# Revit family: Oil_Interceptors-Integral_Storage_Compartment-Jay R. Smith-8599_Series
name_source: partatom
category: Specialty Equipment
units: mm (PartAtom-declared; Revit-internal decimal feet)

## family parameters
Cut with Voids When Loaded = No
Host = Face
OmniClass Number = 23.70.50.11.14.11
OmniClass Title = Oil-Water Separators
Part Type = Normal
Room Calculation Point = No
Round Connector Dimension = Use Diameter
Shared = No

## types (17) — shared parameters
4"(100) Cleanout Access = No
Assembly Code = D2090300
CW Connection = No
Default Elevation = 0"
Description = Oil Interceptors with Integral Storage Compartment
Double Wall Containment - DWC (Note 1) = No
Extension -E (Specify Height eg -E12 for 12" ext.) = No
Finish = Steel-Jay R. Smith-Fabricated
HW Connection = No
High Level Sensor and Control Panel -CBS = No
Installation Type = Floor Mounted
Manufacturer = Jay R. Smith
Manufacturer Product Line = Drainage Products
Material = Steel-Jay R. Smith-Fabricated
Product Documentation Link = https://www.jrsmith.com
Product Page URL = https://www.jrsmith.com
R1 = 2"
Traffic Rated Cover -H20 = No
URL = https://www.jrsmith.com
Vent Connection = No
Vent Connection Diameter = 3"
Waste Connection = Yes

## per-type parameters (varying)
| type | A Dimension | B Dimension | C Dimension | Capacity | D Dimension | E Dimension | F Dimension | Flow Rate | G Dimension | H Dimension | Inlet Connection Description | Inlet Connection Diameter | Inlet/Outlet Radius | J Dimension | M Dimension | Model | N Dimension | Outlet Connection Description | Outlet Connection Diameter | P Dimension | Q Dimension | R Dimension | R2 | S Dimension |
| 8599-10-5 | 2" | 9 1/2" | 3 3/4" | 10 Gals. | 21 1/4" | 13 1/4" | 13" | 5 GPM | 2" | 9 3/4" | 2" Inlet Connection | 2" | 1" | 9 1/2" | 24" | 8599-10-5 | 21 1/4" | 2" Outlet Connection | 2" | 10 1/4" | 11" | 13 1/4" | 1 1/2" | 9 1/4" |
| 8599-10-50 | 2" | 9 1/2" | 3 3/4" | 10 Gals. | 21 1/4" | 13 1/4" | 13" | 50 GPM | 2" | 9 3/4" | 2" Inlet Connection | 2" | 1" | 9 1/2" | 25" | 8599-10-5 | 30" | 2" Outlet Connection | 2" | 50 3/4" | 12" | 55" | 1 1/2" | 9 1/4" |
| 8599-15-50 | 2" | 12" | 3 1/2" | 15 Gals. | 25" | 15 1/2" | 14" | 50 GPM | 2" | 12" | 2" Inlet Connection | 2" | 1" | 10 1/4" | 26" | 8599-15-50 | 30" | 2" Outlet Connection | 2" | 50 3/4" | 12" | 55" | 1 1/2" | 9 3/4" |
| 8599-20-50 | 3" | 13" | 4" | 20 Gals. | 28 1/2" | 17" | 15 3/4" | 50 GPM | 2" | 13 1/2" | 3" Inlet Connection | 3" | 1 1/2" | 12" | 27 3/4" | 8599-20-50 | 30" | 3" Outlet Connection | 3" | 50 3/4" | 12" | 55" | 2" | 12 1/2" |
| 8599-25-100 | 3" | 15 1/4" | 4 1/2" | 25 Gals. | 30" | 19 3/4" | 16 3/4" | 100 GPM | 2" | 16 1/4" | 3" Inlet Connection | 3" | 1 1/2" | 12 3/4" | 31 3/4" | 8599-25-100 | 50 3/4" | 3" Outlet Connection | 3" | 56 3/4" | 15" | 61" | 2" | 13 1/2" |
| 8599-35-100 | 3" | 16" | 5" | 35 Gals. | 32 1/2" | 21" | 18 1/4" | 100 GPM | 2" | 17 1/2" | 3" Inlet Connection | 3" | 1 1/2" | 14 1/2" | 33 1/4" | 8599-35-100 | 50 3/4" | 3" Outlet Connection | 3" | 56 3/4" | 15" | 61" | 2" | 14" |
| 8599-50-100 | 3" | 17 1/2" | 6 3/4" | 50 Gals. | 35 1/2" | 24 1/4" | 20 3/4" | 100 GPM | 2" | 20 3/4" | 3" Inlet Connection | 3" | 1 1/2" | 16" | 35 3/4" | 8599-50-100 | 50 3/4" | 3" Outlet Connection | 3" | 56 3/4" | 15" | 61" | 2" | 16 3/4" |
| 8599-75-100 | 4" | 21 1/2" | 15 1/2" | 75 Gals. | 50 3/4" | 37" | 30 1/2" | 100 GPM | 3" | 32 3/4" | 4" Inlet Connection | 4" | 2" | 21" | 45 1/2" | 8599-75-100 | 50 3/4" | 4" Outlet Connection | 4" | 56 3/4" | 15" | 61" | 2 1/2" | 24" |
| 8599-100-250 | 4" | 27" | 16 1/2" | 100 Gals. | 54 3/4" | 43 1/2" | 33 1/2" | 250 GPM | 3" | 39 1/4" | 4" Inlet Connection | 4" | 2" | 23" | 58 1/2" | 8599-100-250 | 60 3/4" | 4" Outlet Connection | 4" | 60 3/4" | 25" | 65" | 2 1/2" | 25" |
| 8599-150-250 | 5" | 33" | 17 1/2" | 150 Gals. | 60 3/4" | 50 1/2" | 38 1/2" | 250 GPM | 4" | 46 1/4" | 5" Inlet Connection | 5" | 2 1/2" | 25 1/2" | 63 1/2" | 8599-150-250 | 60 3/4" | 5" Outlet Connection | 5" | 60 3/4" | 25" | 65" | 3" | 27" |
| 8599-200-250 | 5" | 37" | 17 1/2" | 200 Gals. | 67 3/4" | 54 1/2" | 43 1/2" | 250 GPM | 4" | 50 1/4" | 5" Inlet Connection | 5" | 2 1/2" | 29" | 68 1/2" | 8599-200-250 | 60 3/4" | 5" Outlet Connection | 5" | 60 3/4" | 25" | 65" | 3" | 27" |
| 8599-250-500 | 5" | 40" | 18" | 250 Gals. | 73 3/4" | 58" | 47 1/2" | 500 GPM | 4" | 53 3/4" | 5" Inlet Connection | 5" | 2 1/2" | 32" | 79 1/2" | 8599-250-500 | 90 3/4" | 5" Outlet Connection | 5" | 71 3/4" | 32" | 76" | 3" | 27 1/2" |
| 8599-300-500 | 5" | 43 1/2" | 18" | 300 Gals. | 85 3/4" | 61 1/2" | 54 1/4" | 500 GPM | 4" | 57 1/4" | 5" Inlet Connection | 5" | 2 1/2" | 38" | 86 1/4" | 8599-300-500 | 90 3/4" | 5" Outlet Connection | 5" | 71 3/4" | 32" | 76" | 3" | 27 1/2" |
| 8599-350-500 | 5" | 43 1/2" | 18" | 350 Gals. | 85 3/4" | 61 1/2" | 54 1/2" | 500 GPM | 4" | 57 1/4" | 5" Inlet Connection | 5" | 2 1/2" | 38" | 86 1/2" | 8599-350-500 | 90 3/4" | 5" Outlet Connection | 5" | 71 3/4" | 32" | 76" | 3" | 27 1/2" |
| 8599-400-500 | 6" | 43 1/2" | 18" | 400 Gals. | 85 3/4" | 61 1/2" | 54 1/2" | 500 GPM | 4" | 57 1/4" | 6" Inlet Connection | 6" | 3" | 38" | 86 1/2" | 8599-400-500 | 90 3/4" | 6" Outlet Connection | 6" | 71 3/4" | 32" | 76" | 3 1/2" | 27 1/2" |
| 8599-450-500 | 6" | 48" | 18" | 450 Gals. | 103 1/4" | 66" | 64 1/2" | 500 GPM | 5" | 61 3/4" | 6" Inlet Connection | 6" | 3" | 46" | 96 1/2" | 8599-450-500 | 90 3/4" | 6" Outlet Connection | 6" | 71 3/4" | 32" | 76" | 3 1/2" | 28" |
| 8599-500-750 | 6" | 48" | 18" | 500 Gals. | 103 1/4" | 66" | 64 1/2" | 750 GPM | 5" | 61 3/4" | 6" Inlet Connection | 6" | 3" | 46" | 99 1/2" | 8599-500-750 | 103 1/4" | 6" Outlet Connection | 6" | 83 3/4" | 35" | 88" | 3 1/2" | 28" |

## geometry (parser evidence)
native form markers: Sweep x3
no freeform markers — native parametric forms only
